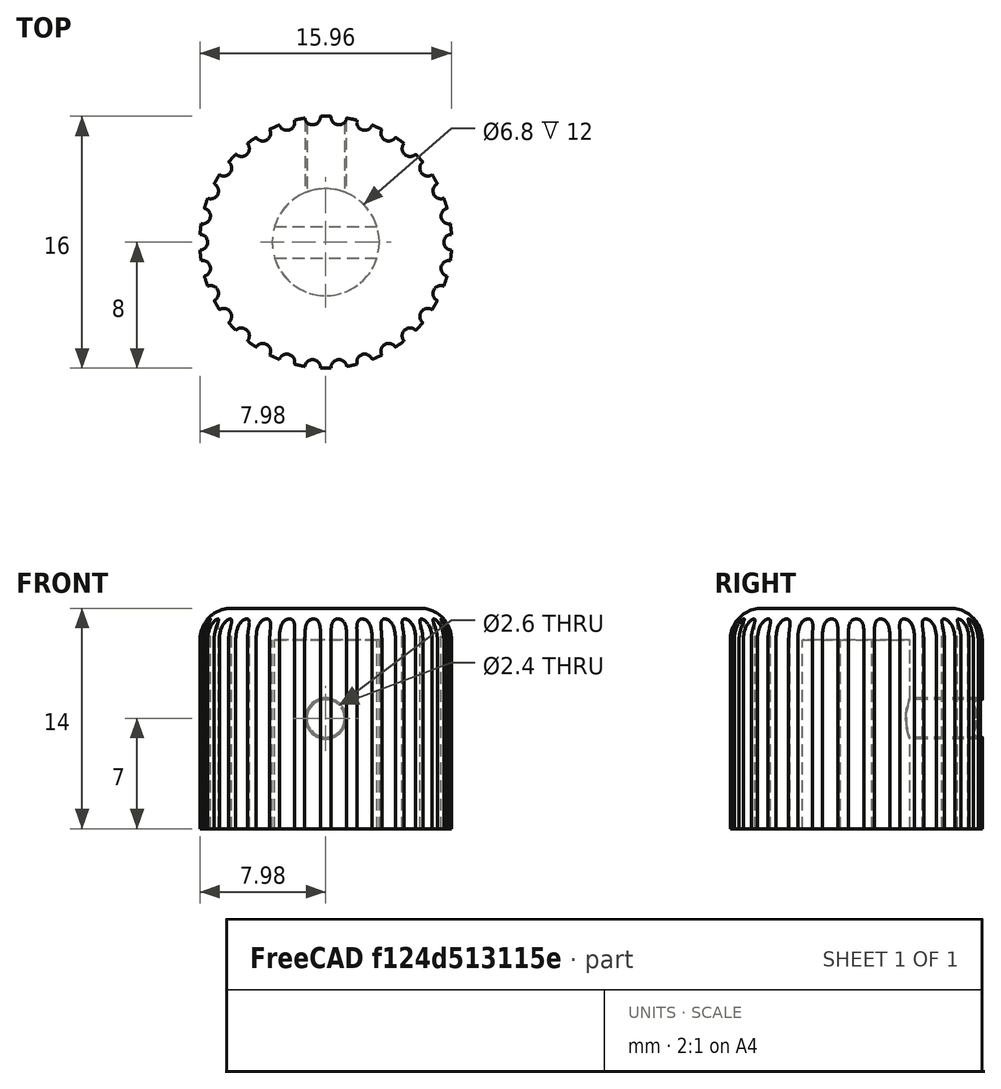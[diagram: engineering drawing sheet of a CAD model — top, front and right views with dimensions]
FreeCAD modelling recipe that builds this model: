
FCSTD DOCUMENT  (FreeCAD 0.17R13522 (Git))
Label: v5_perilla_chica
License: CreativeCommons Attribution-ShareAlike
LicenseURL: http://creativecommons.org/licenses/by-sa/4.0/
objects: Part::Cut×6, Part::Cylinder×4, Part::Fillet×1, Part::FeaturePython×1, Part::Feature×1, Part::Box×1, Part::Fuse×1
note: 15 computed .brp shape members not serialized (recipe doc carries the construction recipe); baked Part::Feature solids carry a one-line shape summary decoded from their .brp

FEATURE [Part::Cylinder] Cylinder
  Angle = 360
  AttacherType = Attacher::AttachEngine3D
  Height = 14
  Radius = 8
FEATURE [Part::Cylinder] Cylinder001  label="perfora centro"
  Angle = 360
  AttacherType = Attacher::AttachEngine3D
  Height = 13
  Placement = pos=(0,0,-1) rot=(0,0,1;0rad)
  Radius = 3.4
FEATURE [Part::Cut] Cut
  Base = -> Cylinder
  Refine = true
  Tool = -> Cylinder001
FEATURE [Part::Cylinder] Cylinder002  label="barilla borde"
  Angle = 360
  AttacherType = Attacher::AttachEngine3D
  Height = 20
  Placement = pos=(-8,0,-1) rot=(0,0,1;0rad)
  Radius = 0.5
FEATURE [Part::Fillet] Fillet
  Base = -> Cut
  Edges = 1 edges r=2: [Edge1]
FEATURE [Part::FeaturePython] Array  # Draft array (typed FeaturePython)
  Angle = 360
  ArrayType = 1
  Axis = (0,0,1)
  Base = -> Cylinder002
  Center = (0,0,0)
  Fuse = false
  IntervalAxis = (0,0,0)
  IntervalX = (1,0,0)
  IntervalY = (0,1,0)
  IntervalZ = (0,0,0)
  NumberPolar = 30
  NumberX = 2
  NumberY = 2
  NumberZ = 1
FEATURE [Part::Cut] Cut001  label="boton sin agujeros allen"
  Base = -> Fillet
  Refine = true
  Tool = -> Array
FEATURE [Part::Feature] Cylinder001005001  label="barilla perfora alen001"
  Placement = pos=(0,27,7) rot=(1,0,0;1.5708rad)
  shape: bbox 2.4 x 26 x 2.4 mm, 3 faces (baked)
FEATURE [Part::Cut] Cut002  label="old base con un agujero para allen"
  Base = -> Cut001
  Refine = true
  Tool = -> Cylinder001005001
FEATURE [Part::Cut] Cut003
  Base = -> Fillet
  Refine = true
  Tool = -> Array
FEATURE [Part::Cut] Cut004  label="perilla con un agujero allen"
  Base = -> Cut003
  Refine = true
  Tool = -> Cylinder001005001
FEATURE [Part::Cylinder] Cylinder001005002  label="barilla perforadora 2.6mm diametro"
  Angle = 360
  AttacherType = Attacher::AttachEngine3D
  Height = 20
  Placement = pos=(0,20,7) rot=(1,0,0;1.5708rad)
  Radius = 1.3
FEATURE [Part::Cut] Cut005  label="perilla chica"
  Base = -> Cut004
  Refine = true
  Tool = -> Cylinder001005002
FEATURE [Part::Box] Box  label="Cube"
  AttacherType = Attacher::AttachEngine3D
  Height = 12
  Length = 10
  Placement = pos=(-5,-1,0) rot=(0,0,1;0rad)
  Width = 2
FEATURE [Part::Fuse] Fusion  label="perilla con aletas"
  Base = -> Cut005
  Refine = true
  Tool = -> Box
